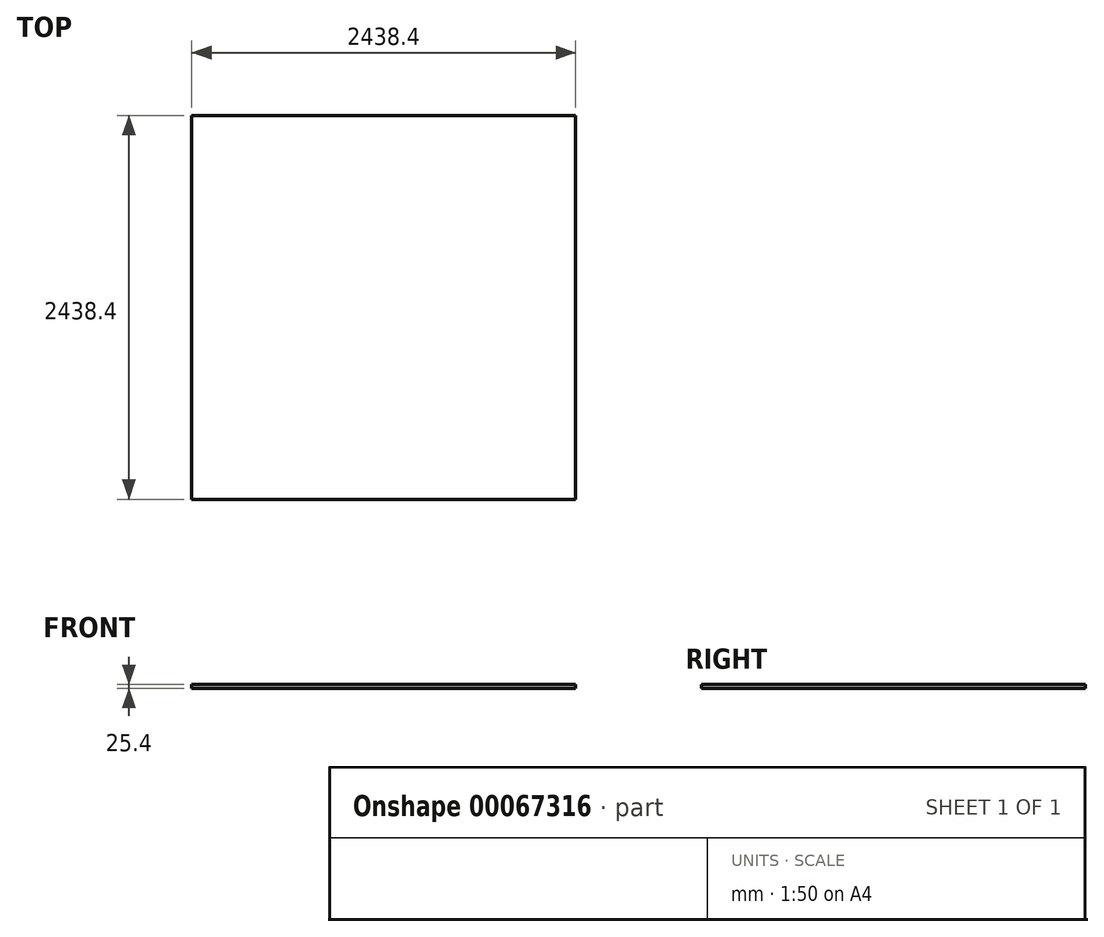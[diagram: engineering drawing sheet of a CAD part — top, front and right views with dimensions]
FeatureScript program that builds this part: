
annotation { "Feature Type Name" : "Feature", "Feature Type Description" : "" }
export const myFeature = defineFeature(function(context is Context, id is Id, definition is map)
    precondition{}
    {
        {
            var Q0;
            Q0=qCreatedBy(makeId("Top.planeOp"),FACE);
            var sketch = newSketch(context, id + "F0", { "sketchPlane" : qUnion([Q0])});
            skLineSegment(sketch, "E0.bottom", {"start": v(-1218.6, 1569.27) * mm, "end": v(1219.8, 1569.27) * mm});
            skLineSegment(sketch, "E0.top", {"start": v(-1218.6, -869.13) * mm, "end": v(1219.8, -869.13) * mm});
            skLineSegment(sketch, "E0.left", {"start": v(-1218.6, 1569.27) * mm, "end": v(-1218.6, -869.13) * mm});
            skLineSegment(sketch, "E0.right", {"start": v(1219.8, 1569.27) * mm, "end": v(1219.8, -869.13) * mm});
            skSolve(sketch);
        }
        {
            var Q0;
            Q0=makeQuery(id+"F0.imprint","IMPRINT",FACE,{"disambiguationData":[TD([[makeQuery(id+"F0.imprint","IMPRINT",EDGE,{"derivedFrom":sQuery(id+"F0.wireOp",EDGE,"E0.bottom")}),-1.0]])]});
            extrude(context, id + "F1", {"entities" : qUnion([Q0]), "depth" : 25.4 * mm});
        }
    });
